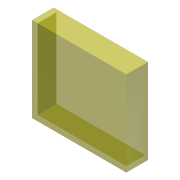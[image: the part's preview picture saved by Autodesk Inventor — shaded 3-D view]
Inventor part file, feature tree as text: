
AUTODESK INVENTOR PART (.ipt)
format: ipt  version: 2014 (Build 180170000, 170)  size: 85,504 bytes
history: native  units: mm
features: extrude x2, sketch x2
ambient origin geometry x8: Origin, YZ Plane, XZ Plane, XY Plane, X Axis, Y Axis, Z Axis, Center Point
bodies: Solid1 (feature_tree)
feature tree (4):
  extrude  "Extrusion1"  Depth=90.0mm
  extrude  "Extrusion2"  Depth=3.0mm
  sketch  "Sketch1"  dims[d0=100.0mm d1=90.0mm]
  sketch  "Sketch2"  dims[d2=3.0mm d3=0.0mm d4=3.0mm d5=3.0mm d6=20.0mm d7=0.0mm]
